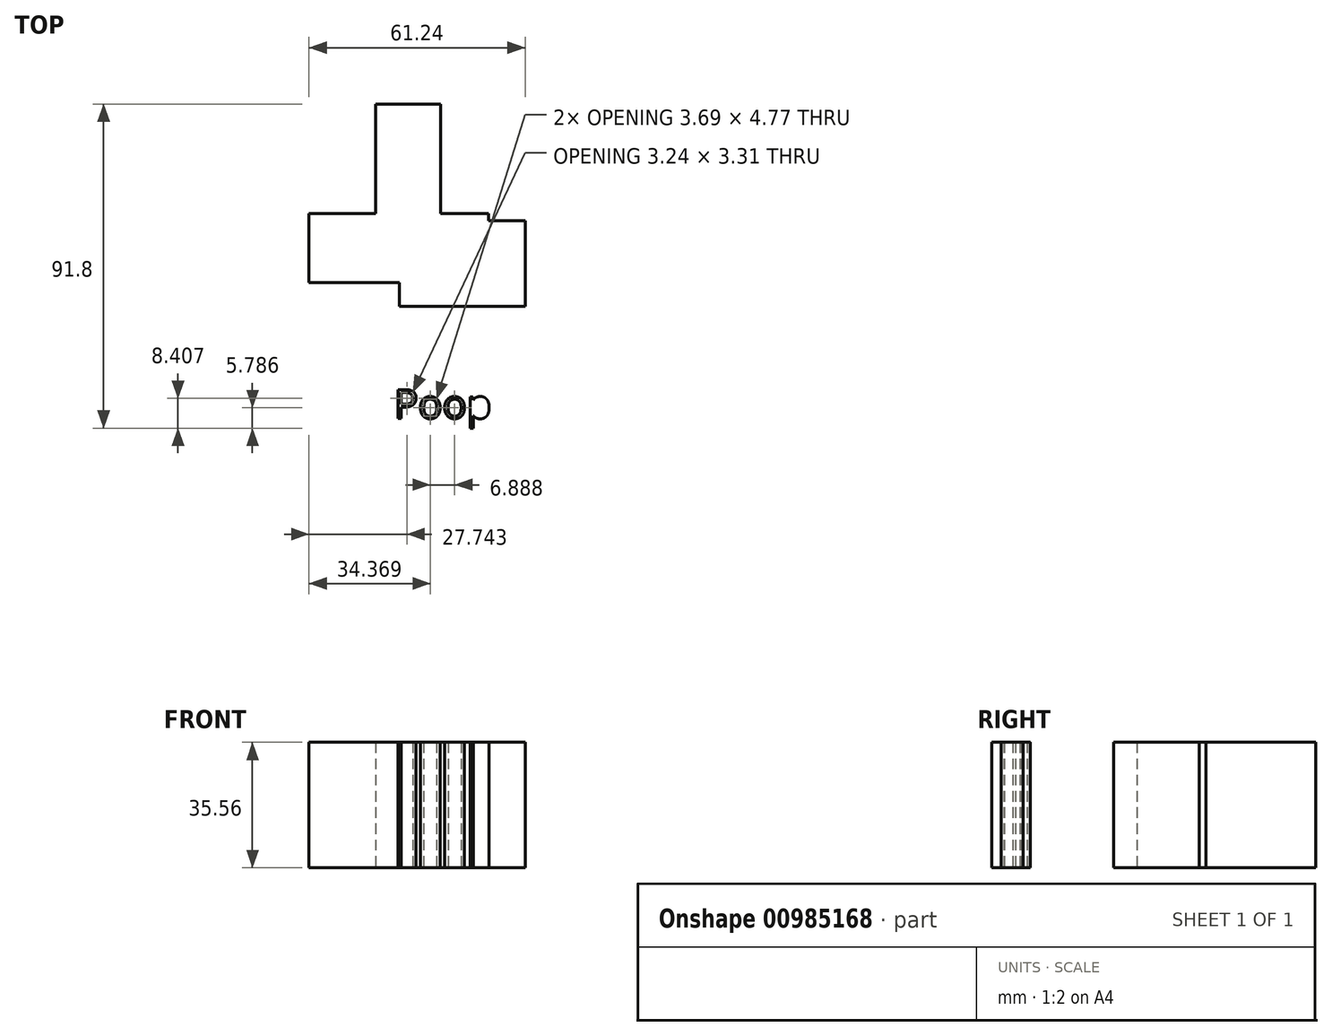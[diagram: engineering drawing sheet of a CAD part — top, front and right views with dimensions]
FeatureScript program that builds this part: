
annotation { "Feature Type Name" : "Feature", "Feature Type Description" : "" }
export const myFeature = defineFeature(function(context is Context, id is Id, definition is map)
    precondition{}
    {
        {
            var Q0;
            Q0=qCreatedBy(makeId("Top.planeOp"),FACE);
            var sketch = newSketch(context, id + "F0", { "sketchPlane" : qUnion([Q0])});
            skLineSegment(sketch, "E0.bottom", {"start": v(-30.58, 24.24) * mm, "end": v(5.05, 24.24) * mm});
            skLineSegment(sketch, "E0.top", {"start": v(-30.58, 0) * mm, "end": v(5.05, 0) * mm});
            skLineSegment(sketch, "E0.left", {"start": v(-30.58, 24.24) * mm, "end": v(-30.58, 0) * mm});
            skLineSegment(sketch, "E0.right", {"start": v(5.05, 24.24) * mm, "end": v(5.05, 0) * mm});
            skLineSegment(sketch, "E1.bottom", {"start": v(-56.19, 26.21) * mm, "end": v(-5.34, 26.21) * mm});
            skLineSegment(sketch, "E1.top", {"start": v(-56.19, 6.64) * mm, "end": v(-5.34, 6.64) * mm});
            skLineSegment(sketch, "E1.left", {"start": v(-56.19, 26.21) * mm, "end": v(-56.19, 6.64) * mm});
            skLineSegment(sketch, "E1.right", {"start": v(-5.34, 26.21) * mm, "end": v(-5.34, 6.64) * mm});
            skLineSegment(sketch, "E2.bottom", {"start": v(-37.25, 57.26) * mm, "end": v(-18.94, 57.26) * mm});
            skLineSegment(sketch, "E2.top", {"start": v(-37.25, 24.24) * mm, "end": v(-18.94, 24.24) * mm});
            skLineSegment(sketch, "E2.left", {"start": v(-37.25, 57.26) * mm, "end": v(-37.25, 24.24) * mm});
            skLineSegment(sketch, "E2.right", {"start": v(-18.94, 57.26) * mm, "end": v(-18.94, 24.24) * mm});
            skText(sketch, "E3", { "text": "Poop", "fontName": "OpenSans-Regular.ttf"});
            const initialGuessF0  = {"E3": [-0.03213, -0.0318, 1, 0, 0.00821]};
            skSetInitialGuess(sketch, initialGuessF0);
            skSolve(sketch);
        }
        {
            var Q0;
            {var subQ2=sQuery(id+"F0.wireOp",EDGE,"E0.top");Q0=makeQuery(id+"F0.imprint","IMPRINT",FACE,{"disambiguationData":[TD([[makeQuery(id+"F0.imprint","IMPRINT",EDGE,{"derivedFrom":subQ2}),1.0]])]});}
            var Q1;
            {var subQ5=sQuery(id+"F0.wireOp",EDGE,"E2.bottom");Q1=makeQuery(id+"F0.imprint","IMPRINT",FACE,{"disambiguationData":[TD([[makeQuery(id+"F0.imprint","IMPRINT",EDGE,{"derivedFrom":subQ5}),-1.0]])]});}
            var Q2;
            Q2=makeQuery(id+"F0.imprint","IMPRINT",FACE,{"disambiguationData":[TD([[makeQuery(id+"F0.imprint","IMPRINT",EDGE,{"derivedFrom":sQuery(id+"F0.wireOp",EDGE,"E3.sketch_text.stroke-0")}),-1.0]])]});
            var Q3;
            Q3=makeQuery(id+"F0.imprint","IMPRINT",FACE,{"disambiguationData":[TD([[makeQuery(id+"F0.imprint","IMPRINT",EDGE,{"derivedFrom":sQuery(id+"F0.wireOp",EDGE,"E3.sketch_text.stroke-15")}),-1.0]])]});
            var Q4;
            Q4=makeQuery(id+"F0.imprint","IMPRINT",FACE,{"disambiguationData":[TD([[makeQuery(id+"F0.imprint","IMPRINT",EDGE,{"derivedFrom":sQuery(id+"F0.wireOp",EDGE,"E3.sketch_text.stroke-32")}),-1.0]])]});
            var Q5;
            Q5=makeQuery(id+"F0.imprint","IMPRINT",FACE,{"disambiguationData":[TD([[makeQuery(id+"F0.imprint","IMPRINT",EDGE,{"derivedFrom":sQuery(id+"F0.wireOp",EDGE,"E3.sketch_text.stroke-49")}),-1.0]])]});
            var Q6;
            {var subQ3=sQuery(id+"F0.wireOp",EDGE,"E1.right");var subQ5=sQuery(id+"F0.wireOp",EDGE,"E1.bottom");var subQ7=makeQuery(id+"F0.imprint","INTERSECT",VERTEX,{"derivedFrom":[subQ5,subQ3]});Q6=makeQuery(id+"F0.imprint","IMPRINT",FACE,{"disambiguationData":[TD([[makeQuery(id+"F0.imprint","IMPRINT",EDGE,{"disambiguationData":[TD([[subQ7,1.0]])],"derivedFrom":subQ5}),-1.0]])]});}
            var Q7;
            {var subQ0=sQuery(id+"F0.wireOp",EDGE,"E1.left");Q7=makeQuery(id+"F0.imprint","IMPRINT",FACE,{"disambiguationData":[TD([[makeQuery(id+"F0.imprint","IMPRINT",EDGE,{"derivedFrom":subQ0}),1.0]])]});}
            var Q8;
            {var subQ5=sQuery(id+"F0.wireOp",EDGE,"E2.top");var subQ6=sQuery(id+"F0.wireOp",EDGE,"E0.left");var subQ7=makeQuery(id+"F0.imprint","INTERSECT",VERTEX,{"derivedFrom":[subQ6,subQ5]});Q8=makeQuery(id+"F0.imprint","IMPRINT",FACE,{"disambiguationData":[TD([[makeQuery(id+"F0.imprint","IMPRINT",EDGE,{"disambiguationData":[TD([[subQ7,-1.0]])],"derivedFrom":subQ6}),1.0]])]});}
            var Q9;
            {var subQ0=sQuery(id+"F0.wireOp",EDGE,"E2.left");var subQ3=sQuery(id+"F0.wireOp",EDGE,"E1.bottom");var subQ4=makeQuery(id+"F0.imprint","INTERSECT",VERTEX,{"derivedFrom":[subQ3,subQ0]});Q9=makeQuery(id+"F0.imprint","IMPRINT",FACE,{"disambiguationData":[TD([[makeQuery(id+"F0.imprint","IMPRINT",EDGE,{"disambiguationData":[TD([[subQ4,-1.0]])],"derivedFrom":subQ3}),-1.0]])]});}
            var Q10;
            Q10=makeQuery(id+"F0.imprint","IMPRINT",FACE,{"disambiguationData":[TD([[makeQuery(id+"F0.imprint","IMPRINT",EDGE,{"derivedFrom":sQuery(id+"F0.wireOp",EDGE,"E3.sketch_text.stroke-65")}),1.0]])]});
            extrude(context, id + "F1", {"entities" : qUnion([Q0, Q1, Q2, Q3, Q4, Q5, Q6, Q7, Q8, Q9, Q10]), "endBound" : BoundingType.SYMMETRIC, "depth" : 35.56 * mm, "offsetDistance" : 25.4 * mm});
        }
    });
